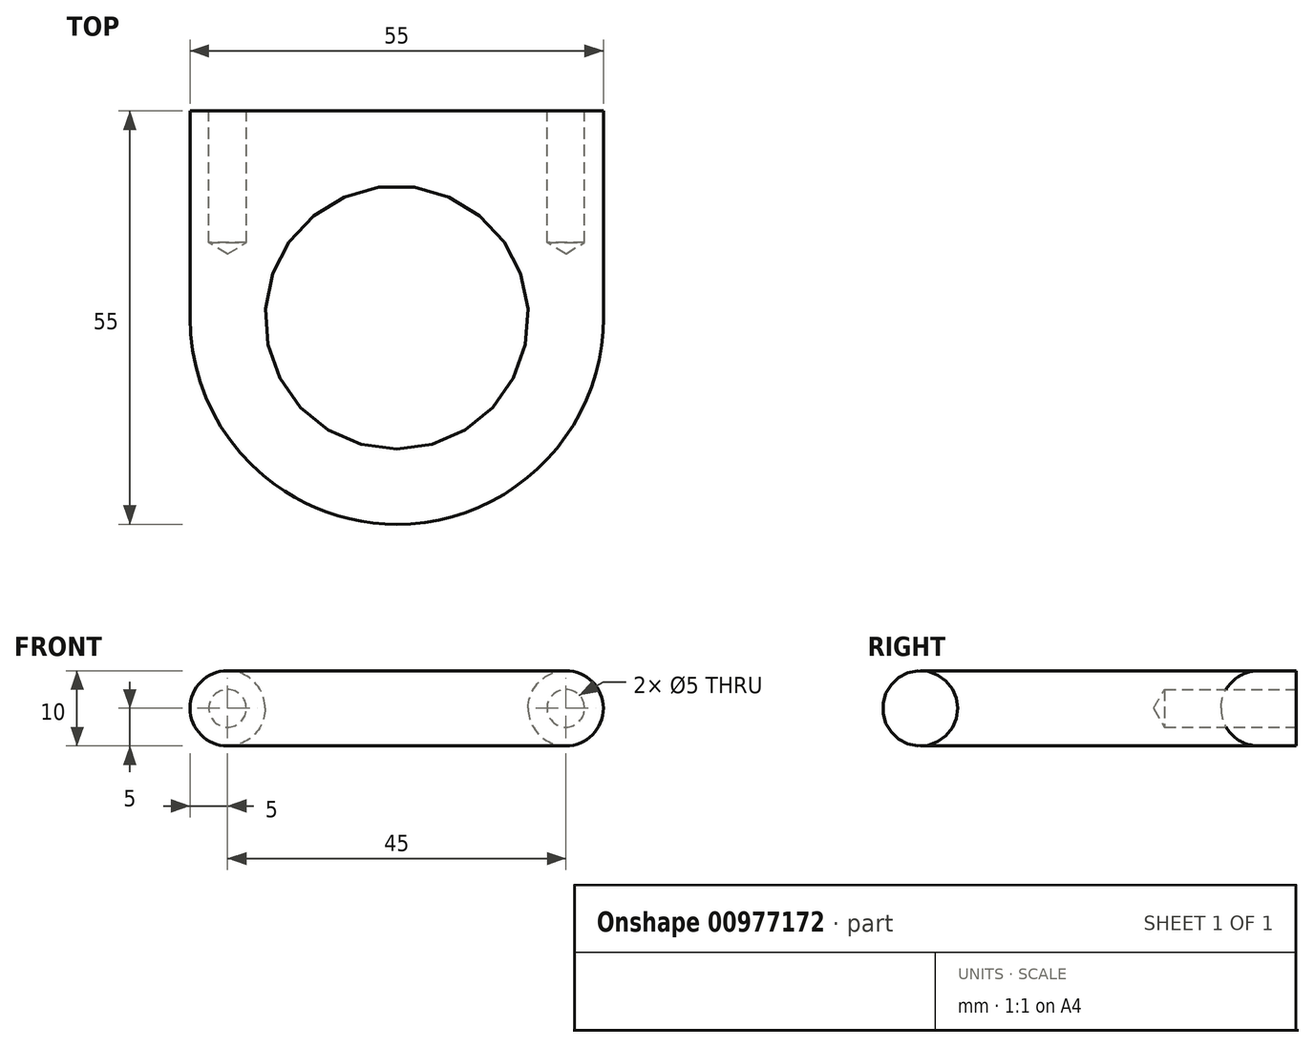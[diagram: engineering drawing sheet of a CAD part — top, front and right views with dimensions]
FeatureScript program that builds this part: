
annotation { "Feature Type Name" : "Feature", "Feature Type Description" : "" }
export const myFeature = defineFeature(function(context is Context, id is Id, definition is map)
    precondition{}
    {
        {
            assignVariable(context, id + "F0", {"name" : "InnerRadius", "anyValue" : 35});
        }
        {
            var Q0;
            Q0=qCreatedBy(makeId("Top.planeOp"),FACE);
            var sketch = newSketch(context, id + "F1", { "sketchPlane" : qUnion([Q0])});
            skCircle(sketch, "E0", {"center": v(0, 0) * mm, "radius": 17.5 * mm});
            skArc(sketch, "E1.0", {"start": v(-27.5, 0) * mm, "mid": v(0, -27.5) * mm, "end": v(27.5, 0) * mm});
            skLineSegment(sketch, "E2", {"start": v(-27.5, 0) * mm, "end": v(27.5, 0) * mm});
            skLineSegment(sketch, "E3", {"start": v(-27.5, 0) * mm, "end": v(-27.5, 27.5) * mm});
            skLineSegment(sketch, "E4", {"start": v(0, 27.5) * mm, "end": v(-27.5, 27.5) * mm});
            skLineSegment(sketch, "E5", {"start": v(27.5, 0) * mm, "end": v(27.5, 27.5) * mm});
            skLineSegment(sketch, "E6", {"start": v(0, 27.5) * mm, "end": v(27.5, 27.5) * mm});
            skSolve(sketch);
        }
        {
            var Q0;
            Q0=makeQuery(id+"F1.imprint","IMPRINT",FACE,{"disambiguationData":[TD([[makeQuery(id+"F1.imprint","IMPRINT",EDGE,{"derivedFrom":sQuery(id+"F1.wireOp",EDGE,"E0")}),-1.0]])]});
            var Q1;
            {var subQ0=sQuery(id+"F1.wireOp",EDGE,"E3");Q1=makeQuery(id+"F1.imprint","IMPRINT",FACE,{"disambiguationData":[TD([[makeQuery(id+"F1.imprint","IMPRINT",EDGE,{"derivedFrom":subQ0}),-1.0]])]});}
            extrude(context, id + "F2", {"entities" : qUnion([Q0, Q1]), "endBound" : BoundingType.SYMMETRIC, "depth" : 10 * mm, "offsetDistance" : 25 * mm});
        }
        {
            var Q0;
            Q0=makeQuery(id+"F2.opExtrude","CAP_EDGE",EDGE,{"disambiguationData":[OSD([sQuery(id+"F1.wireOp",EDGE,"E0")])],"isStart":true});
            var Q1;
            Q1=makeQuery(id+"F2.opExtrude","CAP_EDGE",EDGE,{"disambiguationData":[OSD([sQuery(id+"F1.wireOp",EDGE,"E1.0")])],"isStart":true});
            var Q2;
            Q2=makeQuery(id+"F2.opExtrude","CAP_EDGE",EDGE,{"disambiguationData":[OSD([sQuery(id+"F1.wireOp",EDGE,"E1.0")])],"isStart":false});
            var Q3;
            Q3=makeQuery(id+"F2.opExtrude","CAP_EDGE",EDGE,{"disambiguationData":[OSD([sQuery(id+"F1.wireOp",EDGE,"E0")])],"isStart":false});
            fillet(context, id + "F3", {"entities" : qUnion([Q0, Q1, Q2, Q3]), "radius" : 5 * mm, "tangentPropagation" : true, "allowEdgeOverflow" : false});
        }
        {
            var Q0;
            Q0=makeQuery(id+"F2.opExtrude","SWEPT_FACE",FACE,{"disambiguationData":[OSD([sQuery(id+"F1.wireOp",EDGE,"E4"),sQuery(id+"F1.wireOp",EDGE,"E6")])]});
            var sketch = newSketch(context, id + "F4", { "sketchPlane" : qUnion([Q0])});
            skLineSegment(sketch, "E7", {"start": v(-22.5, 5) * mm, "end": v(-22.5, -5) * mm, "construction": true});
            skLineSegment(sketch, "E8", {"start": v(22.5, 5) * mm, "end": v(22.5, -5) * mm, "construction": true});
            skPoint(sketch, "E9", {"position": v(-22.5, 0) * mm});
            skPoint(sketch, "E10", {"position": v(22.5, 0) * mm});
            skLineSegment(sketch, "E11", {"start": v(0, 5) * mm, "end": v(0, -5) * mm, "construction": true});
            skSolve(sketch);
        }
        {
            var Q0;
            Q0=sQuery(id+"F4.wireOp",VERTEX,"E9");
            var Q1;
            Q1=makeQuery(id+"F2.opExtrude","SWEPT_BODY",BODY,{"disambiguationData":[OSD([sQuery(id+"F1.wireOp",EDGE,"E0"),sQuery(id+"F1.wireOp",EDGE,"E1.0"),sQuery(id+"F1.wireOp",EDGE,"E3"),sQuery(id+"F1.wireOp",EDGE,"E4"),sQuery(id+"F1.wireOp",EDGE,"E5"),sQuery(id+"F1.wireOp",EDGE,"E6")])]});
            hole(context, id + "F5", {"style" : HoleStyle.SIMPLE, "endStyle" : HoleEndStyle.BLIND, "holeDiameter" : 5 * mm, "majorDiameter" : 5 * mm, "holeDepth" : (getVariable(context, 'InnerRadius') / 2) * mm, "isTappedThrough" : true, "tappedDepth" : 12 * mm, "tapClearance" : 3, "locations" : qUnion([Q0]), "scope" : qUnion([Q1])});
        }
        {
            var Q0;
            Q0=sQuery(id+"F4.wireOp",VERTEX,"E10");
            var Q1;
            Q1=makeQuery(id+"F2.opExtrude","SWEPT_BODY",BODY,{"disambiguationData":[OSD([sQuery(id+"F1.wireOp",EDGE,"E0"),sQuery(id+"F1.wireOp",EDGE,"E1.0"),sQuery(id+"F1.wireOp",EDGE,"E3"),sQuery(id+"F1.wireOp",EDGE,"E4"),sQuery(id+"F1.wireOp",EDGE,"E5"),sQuery(id+"F1.wireOp",EDGE,"E6")])]});
            hole(context, id + "F6", {"style" : HoleStyle.SIMPLE, "endStyle" : HoleEndStyle.BLIND, "holeDiameter" : 5 * mm, "majorDiameter" : 5 * mm, "holeDepth" : (getVariable(context, 'InnerRadius') / 2) * mm, "isTappedThrough" : true, "tappedDepth" : 12 * mm, "tapClearance" : 3, "locations" : qUnion([Q0]), "scope" : qUnion([Q1])});
        }
    });
